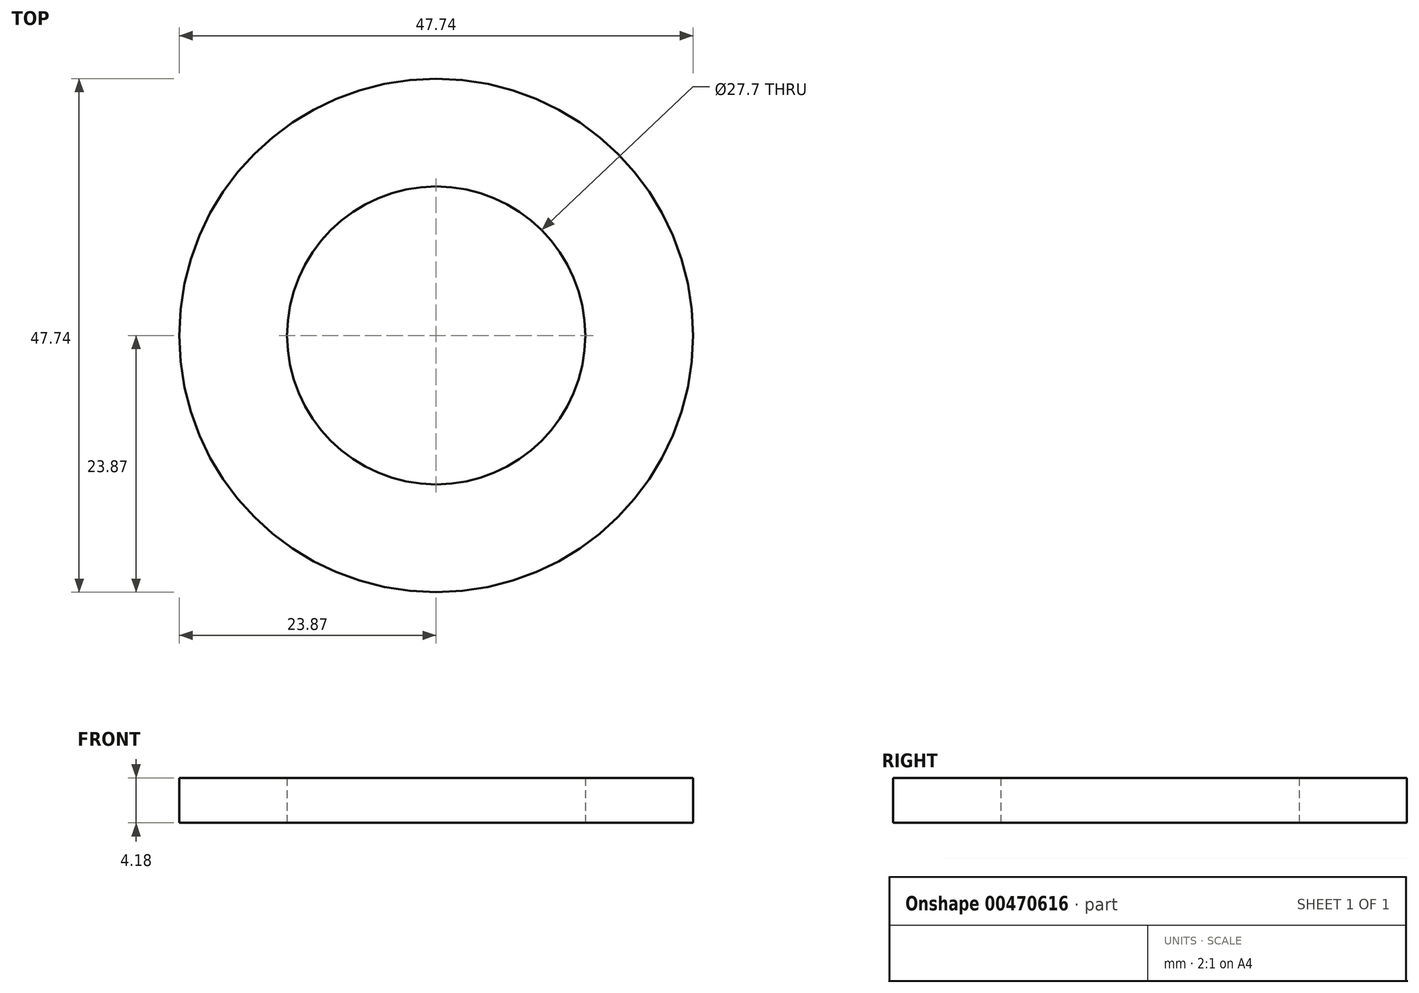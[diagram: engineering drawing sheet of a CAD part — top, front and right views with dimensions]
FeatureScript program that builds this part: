
annotation { "Feature Type Name" : "Feature", "Feature Type Description" : "" }
export const myFeature = defineFeature(function(context is Context, id is Id, definition is map)
    precondition{}
    {
        {
            var Q0;
            Q0=qCreatedBy(makeId("Top.planeOp"),FACE);
            var sketch = newSketch(context, id + "F0", { "sketchPlane" : qUnion([Q0])});
            skCircle(sketch, "E0", {"center": v(0, 0) * mm, "radius": 13.85 * mm});
            skCircle(sketch, "E1", {"center": v(0, 0) * mm, "radius": 23.87 * mm});
            skSolve(sketch);
        }
        {
            var Q0;
            Q0 = qSketchRegion(id + "F0", true);
            extrude(context, id + "F1", {"entities" : qUnion([Q0]), "depth" : 4.18 * mm});
        }
    });
